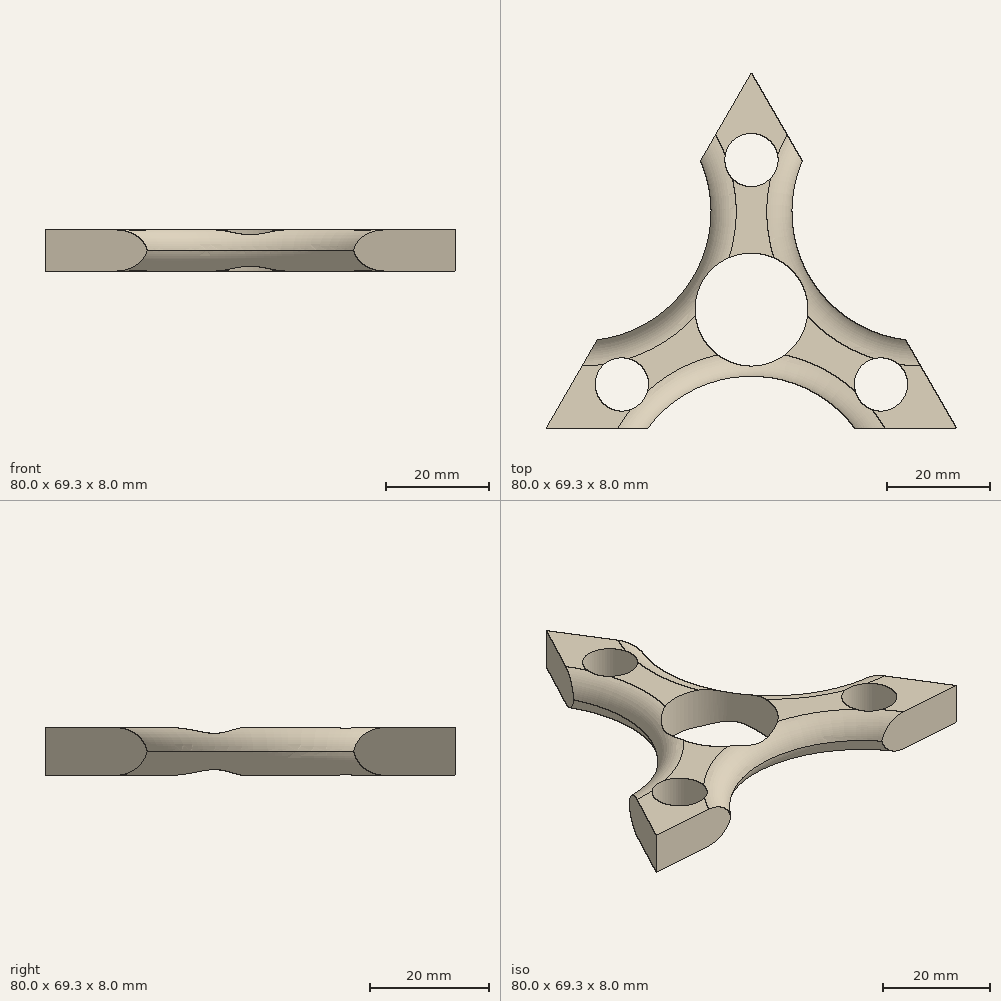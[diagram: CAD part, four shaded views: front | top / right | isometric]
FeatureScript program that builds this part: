
annotation { "Feature Type Name" : "Feature", "Feature Type Description" : "" }
export const myFeature = defineFeature(function(context is Context, id is Id, definition is map)
    precondition{}
    {
        {
            var Q0;
            Q0=qCreatedBy(makeId("Top.planeOp"),FACE);
            var sketch = newSketch(context, id + "F0", { "sketchPlane" : qUnion([Q0])});
            skLineSegment(sketch, "E0", {"start": v(0, 45.76) * mm, "end": v(-40, -23.53) * mm});
            skLineSegment(sketch, "E1", {"start": v(-40, -23.53) * mm, "end": v(40, -23.53) * mm});
            skLineSegment(sketch, "E2", {"start": v(40, -23.53) * mm, "end": v(0, 45.76) * mm});
            skLineSegment(sketch, "E3", {"start": v(-40, -23.53) * mm, "end": v(20, 11.12) * mm, "construction": true});
            skLineSegment(sketch, "E4", {"start": v(40, -23.53) * mm, "end": v(-20, 11.12) * mm, "construction": true});
            skCircle(sketch, "E5", {"center": v(0, -0.43) * mm, "radius": 11 * mm});
            skArc(sketch, "E6", {"start": v(20, -23.53) * mm, "mid": v(0, -13.53) * mm, "end": v(-20, -23.53) * mm});
            skArc(sketch, "E7", {"start": v(10, 28.44) * mm, "mid": v(11.34, 6.12) * mm, "end": v(30, -6.2) * mm});
            skArc(sketch, "E8", {"start": v(-30, -6.2) * mm, "mid": v(-11.34, 6.12) * mm, "end": v(-10, 28.44) * mm});
            skCircle(sketch, "E9", {"center": v(-25.28, -15.03) * mm, "radius": 5.2 * mm});
            skCircle(sketch, "E10.MirrorC", {"center": v(25.28, -15.03) * mm, "radius": 5.2 * mm});
            skCircle(sketch, "E11", {"center": v(0, 28.76) * mm, "radius": 5.2 * mm});
            skSolve(sketch);
        }
        {
            var Q0;
            Q0=makeQuery(id+"F0.imprint","IMPRINT",FACE,{"disambiguationData":[TD([[makeQuery(id+"F0.imprint","IMPRINT",EDGE,{"derivedFrom":sQuery(id+"F0.wireOp",EDGE,"E5")}),-1.0]])]});
            var Q1;
            Q1=sQuery(id+"F0.wireOp",EDGE,"E3");
            var Q2;
            Q2=sQuery(id+"F0.wireOp",EDGE,"E4");
            extrude(context, id + "F1", {"entities" : qUnion([Q0]), "surfaceEntities" : qUnion([Q1, Q2]), "depth" : 8 * mm, "offsetDistance" : 25 * mm});
        }
        {
            var Q0;
            Q0=makeQuery(id+"F1.opExtrude","CAP_EDGE",EDGE,{"disambiguationData":[OSD([sQuery(id+"F0.wireOp",EDGE,"E8")])],"isStart":false});
            var Q1;
            Q1=makeQuery(id+"F1.opExtrude","CAP_EDGE",EDGE,{"disambiguationData":[OSD([sQuery(id+"F0.wireOp",EDGE,"E7")])],"isStart":false});
            var Q2;
            Q2=makeQuery(id+"F1.opExtrude","CAP_EDGE",EDGE,{"disambiguationData":[OSD([sQuery(id+"F0.wireOp",EDGE,"E6")])],"isStart":false});
            var Q3;
            Q3=makeQuery(id+"F1.opExtrude","CAP_EDGE",EDGE,{"disambiguationData":[OSD([sQuery(id+"F0.wireOp",EDGE,"E8")])],"isStart":true});
            var Q4;
            Q4=makeQuery(id+"F1.opExtrude","CAP_EDGE",EDGE,{"disambiguationData":[OSD([sQuery(id+"F0.wireOp",EDGE,"E7")])],"isStart":true});
            var Q5;
            Q5=makeQuery(id+"F1.opExtrude","CAP_EDGE",EDGE,{"disambiguationData":[OSD([sQuery(id+"F0.wireOp",EDGE,"E6")])],"isStart":true});
            fillet(context, id + "F2", {"entities" : qUnion([Q0, Q1, Q2, Q3, Q4, Q5]), "radius" : 5 * mm, "tangentPropagation" : true, "allowEdgeOverflow" : false});
        }
    });
